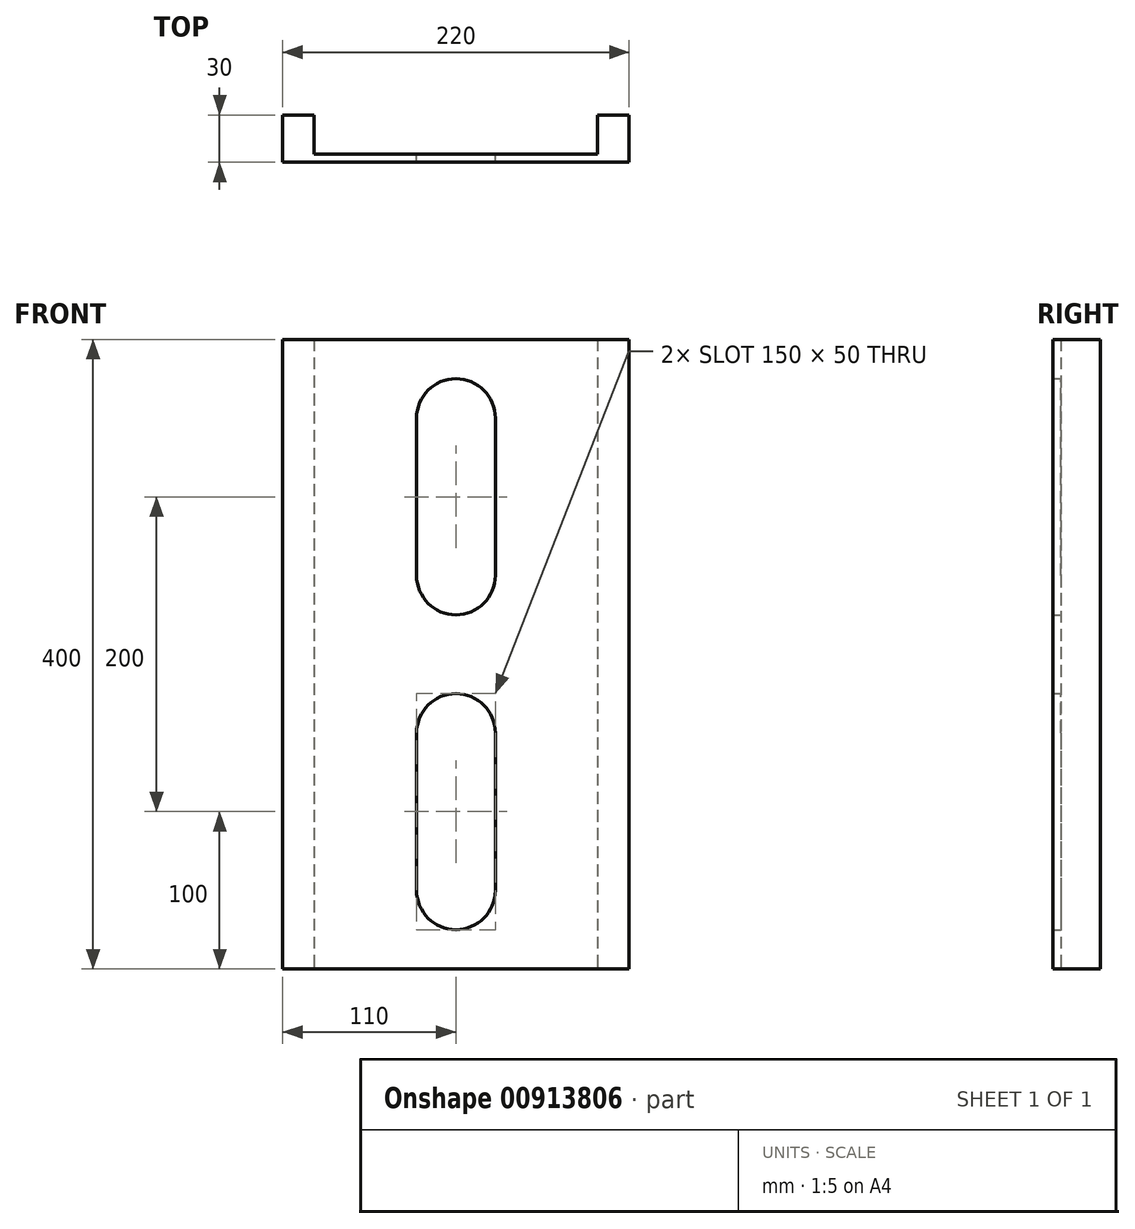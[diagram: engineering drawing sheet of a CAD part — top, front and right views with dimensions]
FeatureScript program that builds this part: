
annotation { "Feature Type Name" : "Feature", "Feature Type Description" : "" }
export const myFeature = defineFeature(function(context is Context, id is Id, definition is map)
    precondition{}
    {
        {
            var Q0;
            Q0=qCreatedBy(makeId("Top.planeOp"),FACE);
            var sketch = newSketch(context, id + "F0", { "sketchPlane" : qUnion([Q0])});
            skLineSegment(sketch, "E0.bottom", {"start": v(-110, -15) * mm, "end": v(110, -15) * mm});
            skLineSegment(sketch, "E0.top", {"start": v(-110, 15) * mm, "end": v(-90, 15) * mm});
            skLineSegment(sketch, "E0.left", {"start": v(-110, -15) * mm, "end": v(-110, 15) * mm});
            skLineSegment(sketch, "E0.right", {"start": v(110, -15) * mm, "end": v(110, 15) * mm});
            skPoint(sketch, "E0.middle", {"position": v(0, 0) * mm});
            skLineSegment(sketch, "E1.top", {"start": v(-90, -10) * mm, "end": v(90, -10) * mm});
            skLineSegment(sketch, "E1.left", {"start": v(-90, 15) * mm, "end": v(-90, -10) * mm});
            skLineSegment(sketch, "E1.right", {"start": v(90, 15) * mm, "end": v(90, -10) * mm});
            skLineSegment(sketch, "E2.trimOffspring", {"start": v(90, 15) * mm, "end": v(110, 15) * mm});
            skSolve(sketch);
        }
        {
            var Q0;
            Q0=makeQuery(id+"F0.imprint","IMPRINT",FACE,{"disambiguationData":[TD([[makeQuery(id+"F0.imprint","IMPRINT",EDGE,{"derivedFrom":sQuery(id+"F0.wireOp",EDGE,"E0.bottom")}),1.0]])]});
            extrude(context, id + "F1", {"entities" : qUnion([Q0]), "depth" : 400 * mm, "offsetDistance" : 25 * mm});
        }
        {
            var Q0;
            Q0=qCreatedBy(makeId("Front.planeOp"),FACE);
            var sketch = newSketch(context, id + "F2", { "sketchPlane" : qUnion([Q0])});
            skLineSegment(sketch, "E3.left", {"start": v(-25, 250) * mm, "end": v(-25, 350) * mm});
            skLineSegment(sketch, "E3.right", {"start": v(25, 250) * mm, "end": v(25, 350) * mm});
            skPoint(sketch, "E3.middle", {"position": v(0, 300) * mm});
            skArc(sketch, "E4", {"start": v(-25, 350) * mm, "mid": v(0, 375) * mm, "end": v(25, 350) * mm});
            skArc(sketch, "E5", {"start": v(25, 250) * mm, "mid": v(0, 225) * mm, "end": v(-25, 250) * mm});
            skLineSegment(sketch, "E6", {"start": v(-151.38, 200) * mm, "end": v(155.82, 200) * mm, "construction": true});
            skLineSegment(sketch, "E7.MirrorCS", {"start": v(25, 150) * mm, "end": v(25, 50) * mm});
            skLineSegment(sketch, "E8.MirrorCS", {"start": v(-25, 150) * mm, "end": v(-25, 50) * mm});
            skArc(sketch, "E9.MirrorCS", {"start": v(-25, 50) * mm, "mid": v(0, 25) * mm, "end": v(25, 50) * mm});
            skArc(sketch, "E10.MirrorCS", {"start": v(25, 150) * mm, "mid": v(0, 175) * mm, "end": v(-25, 150) * mm});
            skSolve(sketch);
        }
        {
            var Q0;
            Q0 = qSketchRegion(id + "F2", true);
            extrude(context, id + "F3", {"entities" : qUnion([Q0]), "operationType" : NewBodyOperationType.REMOVE, "depth" : 25 * mm, "offsetDistance" : 25 * mm});
        }
    });
